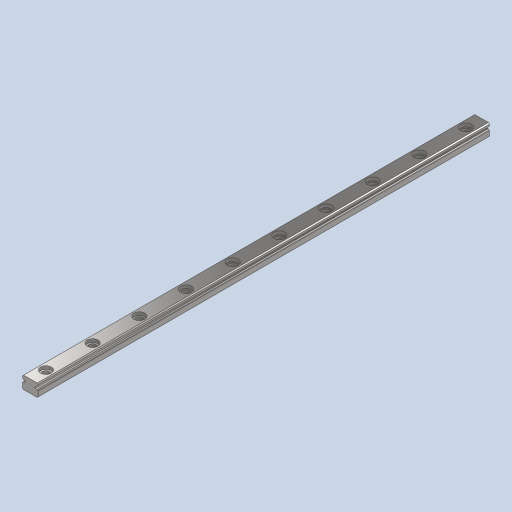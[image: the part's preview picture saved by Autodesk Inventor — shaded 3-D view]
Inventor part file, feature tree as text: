
AUTODESK INVENTOR PART (.ipt)
format: ipt  version: 2023 (Build 270158000, 158)  size: 212,992 bytes
history: native  units: mm
features: other x98, sketch x2, extrude x1, hole x1, pattern_linear x1
ambient origin geometry x8: Origin, YZ Plane, XZ Plane, XY Plane, X Axis, Y Axis, Z Axis, Center Point
bodies: Solid1 (feature_tree)
feature tree (103):
  extrude  "Extrusion1"  Depth=10.0mm TaperAngle=0.0deg
  hole  "Hole1"  [1 undecoded]
  pattern_linear  "Rectangular Pattern1"  [2 undecoded]
  other  "rail_to_adjusting_block_XY"
  other  "rail_to_adjusting_block_YZ"
  other  "rail_to_adjusting_block_ZX"
  other  "rail_to_adjusting_block_X"
  other  "rail_to_adjusting_block_Y"
  other  "rail_to_adjusting_block_Z"
  other  "rail_to_adjusting_block_Center"
  other  "screw_1_XY"
  other  "screw_1_YZ"
  other  "screw_1_ZX"
  other  "screw_1_X"
  other  "screw_1_Y"
  other  "screw_1_Z"
  other  "screw_1_Center"
  other  "screw_10_XY"
  other  "screw_10_YZ"
  other  "screw_10_ZX"
  other  "screw_10_X"
  other  "screw_10_Y"
  other  "screw_10_Z"
  other  "screw_10_Center"
  other  "screw_2_XY"
  other  "screw_2_YZ"
  other  "screw_2_ZX"
  other  "screw_2_X"
  other  "screw_2_Y"
  other  "screw_2_Z"
  other  "screw_2_Center"
  other  "screw_3_XY"
  other  "screw_3_YZ"
  other  "screw_3_ZX"
  other  "screw_3_X"
  other  "screw_3_Y"
  other  "screw_3_Z"
  other  "screw_3_Center"
  other  "screw_4_XY"
  other  "screw_4_YZ"
  other  "screw_4_ZX"
  other  "screw_4_X"
  other  "screw_4_Y"
  other  "screw_4_Z"
  other  "screw_4_Center"
  other  "screw_5_XY"
  other  "screw_5_YZ"
  other  "screw_5_ZX"
  other  "screw_5_X"
  other  "screw_5_Y"
  other  "screw_5_Z"
  other  "screw_5_Center"
  other  "screw_6_XY"
  other  "screw_6_YZ"
  other  "screw_6_ZX"
  other  "screw_6_X"
  other  "screw_6_Y"
  other  "screw_6_Z"
  other  "screw_6_Center"
  other  "screw_7_XY"
  other  "screw_7_YZ"
  other  "screw_7_ZX"
  other  "screw_7_X"
  other  "screw_7_Y"
  other  "screw_7_Z"
  other  "screw_7_Center"
  other  "screw_8_XY"
  other  "screw_8_YZ"
  other  "screw_8_ZX"
  other  "screw_8_X"
  other  "screw_8_Y"
  other  "screw_8_Z"
  other  "screw_8_Center"
  other  "screw_9_XY"
  other  "screw_9_YZ"
  other  "screw_9_ZX"
  other  "screw_9_X"
  other  "screw_9_Y"
  other  "screw_9_Z"
  other  "screw_9_Center"
  other  "to_block_XY"
  other  "to_block_YZ"
  other  "to_block_ZX"
  other  "to_block_X"
  other  "to_block_Y"
  other  "to_block_Z"
  other  "to_block_Center"
  other  "to_block_2_XY"
  other  "to_block_2_YZ"
  other  "to_block_2_ZX"
  other  "to_block_2_X"
  other  "to_block_2_Y"
  other  "to_block_2_Z"
  other  "to_block_2_Center"
  other  "to_kue_XY"
  other  "to_kue_YZ"
  other  "to_kue_ZX"
  other  "to_kue_X"
  other  "to_kue_Y"
  other  "to_kue_Z"
  other  "to_kue_Center"
  sketch  "Sketch_12"  dims[d2=2.4mm d3=6.0mm d4=3.5mm d5=1.0mm d6=90.0deg d7=4.0mm d8=0.0mm d9=100.0mm d11=15.0mm d12=10.0mm d14=0.0mm d15=0.0mm d16=0.0mm d17=0.0mm d18=0.0mm d19=0.0mm d20=0.0mm d21=0.0mm d22=0.0mm d23=0.0mm d24=0.0mm d25=0.0mm d26=0.0mm]
  sketch  "Sketch2"  dims[d0=145.0mm d1=0.0mm]
note: 3 required parameter values undecoded (feature->parameter linkage not recoverable at this tier; creation-order binding heuristic only, values carry confidence <= 0.55)
